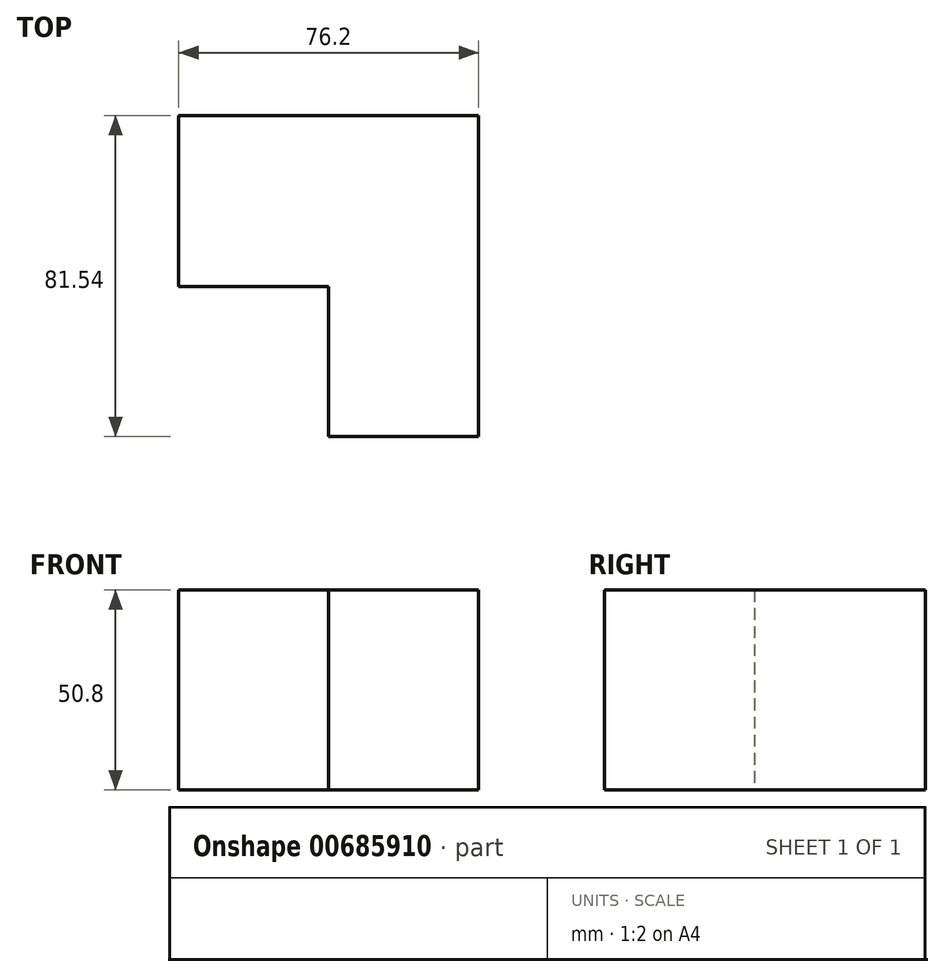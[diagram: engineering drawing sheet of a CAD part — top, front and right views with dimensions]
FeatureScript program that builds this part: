
annotation { "Feature Type Name" : "Feature", "Feature Type Description" : "" }
export const myFeature = defineFeature(function(context is Context, id is Id, definition is map)
    precondition{}
    {
        {
            var Q0;
            Q0=qCreatedBy(makeId("Top.planeOp"),FACE);
            var sketch = newSketch(context, id + "F0", { "sketchPlane" : qUnion([Q0])});
            skLineSegment(sketch, "E0", {"start": v(0, 43.44) * mm, "end": v(-76.2, 43.44) * mm});
            skLineSegment(sketch, "E1", {"start": v(-76.2, 43.44) * mm, "end": v(-76.2, 0) * mm});
            skLineSegment(sketch, "E2", {"start": v(-76.2, 0) * mm, "end": v(-50.8, 0) * mm});
            skLineSegment(sketch, "E3", {"start": v(-50.8, 0) * mm, "end": v(-38.1, 0) * mm});
            skLineSegment(sketch, "E4", {"start": v(-38.1, 0) * mm, "end": v(-38.1, -38.1) * mm});
            skLineSegment(sketch, "E5", {"start": v(-38.1, -38.1) * mm, "end": v(0, -38.1) * mm});
            skLineSegment(sketch, "E6", {"start": v(0, -38.1) * mm, "end": v(0, 43.44) * mm});
            skSolve(sketch);
        }
        {
            var Q0;
            Q0=makeQuery(id+"F0.imprint","IMPRINT",FACE,{"disambiguationData":[TD([[makeQuery(id+"F0.imprint","IMPRINT",EDGE,{"derivedFrom":sQuery(id+"F0.wireOp",EDGE,"E0")}),1.0]])]});
            extrude(context, id + "F1", {"entities" : qUnion([Q0]), "depth" : 50.8 * mm, "offsetDistance" : 25.4 * mm});
        }
    });
